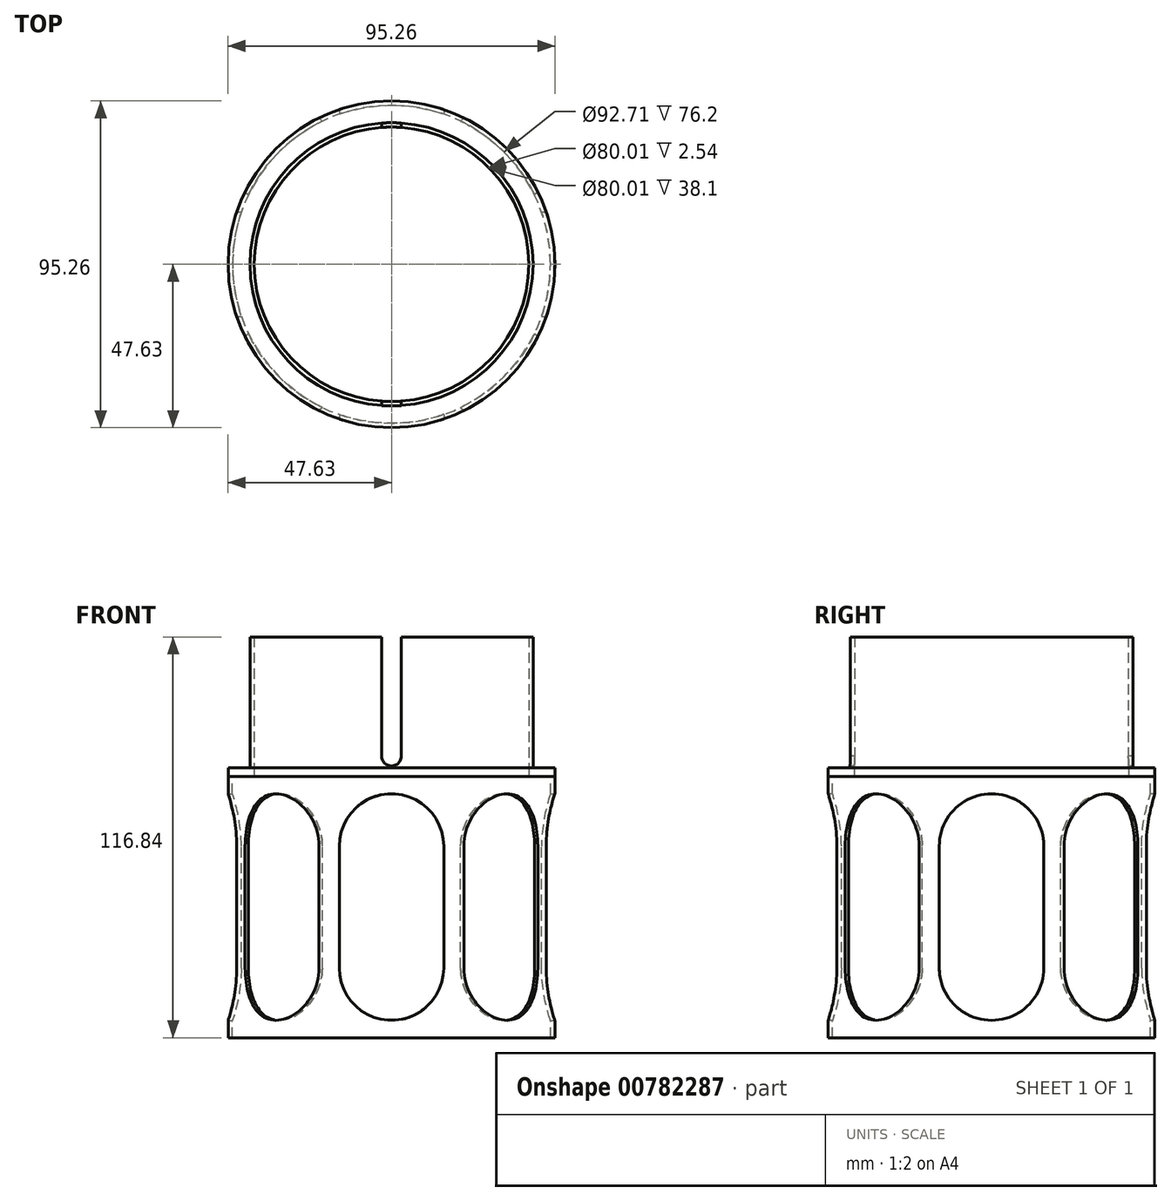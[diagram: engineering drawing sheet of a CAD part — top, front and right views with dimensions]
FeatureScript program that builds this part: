
annotation { "Feature Type Name" : "Feature", "Feature Type Description" : "" }
export const myFeature = defineFeature(function(context is Context, id is Id, definition is map)
    precondition{}
    {
        {
            var Q0;
            Q0=qCreatedBy(makeId("Top.planeOp"),FACE);
            var sketch = newSketch(context, id + "F0", { "sketchPlane" : qUnion([Q0])});
            skCircle(sketch, "E0", {"center": v(0, 0) * mm, "radius": 41.28 * mm});
            skCircle(sketch, "E1", {"center": v(0, 0) * mm, "radius": 40 * mm});
            skCircle(sketch, "E2", {"center": v(0, 0) * mm, "radius": 47.63 * mm});
            skCircle(sketch, "E3", {"center": v(0, 0) * mm, "radius": 46.35 * mm});
            skSolve(sketch);
        }
        {
            var Q0;
            Q0=makeQuery(id+"F0.imprint","IMPRINT",FACE,{"disambiguationData":[TD([[makeQuery(id+"F0.imprint","IMPRINT",EDGE,{"derivedFrom":sQuery(id+"F0.wireOp",EDGE,"E0")}),1.0]])]});
            extrude(context, id + "F1", {"entities" : qUnion([Q0]), "depth" : 40.64 * mm, "offsetDistance" : 25.4 * mm, "hasSecondDirection" : true, "secondDirectionOppositeDirection" : false, "secondDirectionDepth" : 2.54 * mm});
        }
        {
            var Q0;
            Q0=makeQuery(id+"F0.imprint","IMPRINT",FACE,{"disambiguationData":[TD([[makeQuery(id+"F0.imprint","IMPRINT",EDGE,{"derivedFrom":sQuery(id+"F0.wireOp",EDGE,"E2")}),1.0]])]});
            var Q1;
            Q1=sQuery(id+"F0.wireOp",EDGE,"E2");
            var Q2;
            Q2=sQuery(id+"F0.wireOp",EDGE,"E3");
            extrude(context, id + "F2", {"entities" : qUnion([Q0]), "surfaceEntities" : qUnion([Q1, Q2]), "oppositeDirection" : true, "depth" : 76.2 * mm, "offsetDistance" : 25.4 * mm});
        }
        {
            var Q0;
            Q0=makeQuery(id+"F0.imprint","IMPRINT",FACE,{"disambiguationData":[TD([[makeQuery(id+"F0.imprint","IMPRINT",EDGE,{"derivedFrom":sQuery(id+"F0.wireOp",EDGE,"E2")}),1.0]])]});
            var Q1;
            Q1=makeQuery(id+"F0.imprint","IMPRINT",FACE,{"disambiguationData":[TD([[makeQuery(id+"F0.imprint","IMPRINT",EDGE,{"derivedFrom":sQuery(id+"F0.wireOp",EDGE,"E0")}),-1.0]])]});
            var Q2;
            Q2=makeQuery(id+"F0.imprint","IMPRINT",FACE,{"disambiguationData":[TD([[makeQuery(id+"F0.imprint","IMPRINT",EDGE,{"derivedFrom":sQuery(id+"F0.wireOp",EDGE,"E0")}),1.0]])]});
            var Q3;
            Q3=sQuery(id+"F0.wireOp",EDGE,"E2");
            var Q4;
            Q4=sQuery(id+"F0.wireOp",EDGE,"E1");
            extrude(context, id + "F3", {"entities" : qUnion([Q0, Q1, Q2]), "surfaceEntities" : qUnion([Q3, Q4]), "depth" : 2.54 * mm, "offsetDistance" : 25.4 * mm});
        }
        {
            var Q0;
            Q0=qCreatedBy(makeId("Front.planeOp"),FACE);
            var sketch = newSketch(context, id + "F4", { "sketchPlane" : qUnion([Q0])});
            skCircle(sketch, "E4", {"center": v(0, -20.32) * mm, "radius": 15.24 * mm});
            skCircle(sketch, "E5", {"center": v(0, -55.89) * mm, "radius": 15.24 * mm});
            skLineSegment(sketch, "E6", {"start": v(-15.24, -55.89) * mm, "end": v(-15.24, -20.32) * mm});
            skLineSegment(sketch, "E7", {"start": v(15.24, -55.89) * mm, "end": v(15.24, -20.32) * mm});
            skCircle(sketch, "E8", {"center": v(0, 5.88) * mm, "radius": 2.84 * mm});
            skLineSegment(sketch, "E9", {"start": v(2.84, 5.88) * mm, "end": v(2.84, 40.64) * mm});
            skLineSegment(sketch, "E10", {"start": v(-2.84, 5.94) * mm, "end": v(-2.84, 40.64) * mm});
            skLineSegment(sketch, "E11", {"start": v(-2.84, 40.64) * mm, "end": v(2.84, 40.64) * mm});
            skSolve(sketch);
        }
        {
            var Q0;
            {var subQ0=sQuery(id+"F4.wireOp",EDGE,"E5");var subQ1=makeQuery(id+"F4.imprint","INTERSECT",VERTEX,{"derivedFrom":[subQ0,sQuery(id+"F4.wireOp",EDGE,"E6")]});Q0=makeQuery(id+"F4.imprint","IMPRINT",FACE,{"disambiguationData":[TD([[makeQuery(id+"F4.imprint","IMPRINT",EDGE,{"disambiguationData":[TD([[subQ1,1.0]])],"derivedFrom":subQ0}),1.0]])]});}
            var Q1;
            {var subQ0=sQuery(id+"F4.wireOp",EDGE,"E6");Q1=makeQuery(id+"F4.imprint","IMPRINT",FACE,{"disambiguationData":[TD([[makeQuery(id+"F4.imprint","IMPRINT",EDGE,{"derivedFrom":subQ0}),-1.0]])]});}
            var Q2;
            {var subQ0=sQuery(id+"F4.wireOp",EDGE,"E4");var subQ1=makeQuery(id+"F4.imprint","INTERSECT",VERTEX,{"derivedFrom":[subQ0,sQuery(id+"F4.wireOp",EDGE,"E6")]});Q2=makeQuery(id+"F4.imprint","IMPRINT",FACE,{"disambiguationData":[TD([[makeQuery(id+"F4.imprint","IMPRINT",EDGE,{"disambiguationData":[TD([[subQ1,1.0]])],"derivedFrom":subQ0}),1.0]])]});}
            var Q3;
            {var subQ0=sQuery(id+"F4.wireOp",EDGE,"E8");var subQ1=makeQuery(id+"F4.imprint","INTERSECT",VERTEX,{"derivedFrom":[subQ0,sQuery(id+"F4.wireOp",EDGE,"E9")]});Q3=makeQuery(id+"F4.imprint","IMPRINT",FACE,{"disambiguationData":[TD([[makeQuery(id+"F4.imprint","IMPRINT",EDGE,{"disambiguationData":[TD([[subQ1,-1.0]])],"derivedFrom":subQ0}),1.0]])]});}
            var Q4;
            {var subQ0=sQuery(id+"F4.wireOp",EDGE,"E9");Q4=makeQuery(id+"F4.imprint","IMPRINT",FACE,{"disambiguationData":[TD([[makeQuery(id+"F4.imprint","IMPRINT",EDGE,{"derivedFrom":subQ0}),1.0]])]});}
            extrude(context, id + "F5", {"entities" : qUnion([Q0, Q1, Q2, Q3, Q4]), "operationType" : NewBodyOperationType.REMOVE, "oppositeDirection" : true, "depth" : 76.2 * mm, "offsetDistance" : 25.4 * mm, "hasSecondDirection" : true, "secondDirectionOppositeDirection" : false, "secondDirectionDepth" : 76.2 * mm});
        }
        {
            var Q0;
            Q0=qCreatedBy(makeId("Right.planeOp"),FACE);
            var sketch = newSketch(context, id + "F6", { "sketchPlane" : qUnion([Q0])});
            skCircle(sketch, "E12", {"center": v(0, -20.32) * mm, "radius": 15.24 * mm});
            skCircle(sketch, "E13", {"center": v(0, -55.88) * mm, "radius": 15.24 * mm});
            skLineSegment(sketch, "E14", {"start": v(-15.24, -55.88) * mm, "end": v(-15.24, -20.32) * mm});
            skLineSegment(sketch, "E15", {"start": v(15.24, -55.88) * mm, "end": v(15.24, -20.32) * mm});
            skSolve(sketch);
        }
        {
            var Q0;
            Q0=qCreatedBy(makeId("Front.planeOp"),FACE);
            var Q1;
            Q1=qCreatedBy(makeId("Right.planeOp"),FACE);
            cPlane(context, id + "F7", {"entities" : qUnion([Q0, Q1]), "cplaneType" : CPlaneType.MID_PLANE, "offset" : 25.4 * mm, "width" : 152.4 * mm, "height" : 152.4 * mm});
        }
        {
            var Q0;
            Q0=qCreatedBy(id+"F7.planeOp",FACE);
            var sketch = newSketch(context, id + "F8", { "sketchPlane" : qUnion([Q0])});
            skCircle(sketch, "E16", {"center": v(0, -20.32) * mm, "radius": 15.24 * mm});
            skCircle(sketch, "E17", {"center": v(0, -55.88) * mm, "radius": 15.24 * mm});
            skLineSegment(sketch, "E18", {"start": v(-15.24, -55.88) * mm, "end": v(-15.24, -20.32) * mm});
            skLineSegment(sketch, "E19", {"start": v(15.24, -55.88) * mm, "end": v(15.24, -20.32) * mm});
            skSolve(sketch);
        }
        {
            var Q0;
            {var subQ0=sQuery(id+"F8.wireOp",EDGE,"E17");var subQ1=makeQuery(id+"F8.imprint","INTERSECT",VERTEX,{"derivedFrom":[subQ0,sQuery(id+"F8.wireOp",EDGE,"E18")]});Q0=makeQuery(id+"F8.imprint","IMPRINT",FACE,{"disambiguationData":[TD([[makeQuery(id+"F8.imprint","IMPRINT",EDGE,{"disambiguationData":[TD([[subQ1,1.0]])],"derivedFrom":subQ0}),1.0]])]});}
            var Q1;
            {var subQ0=sQuery(id+"F8.wireOp",EDGE,"E18");Q1=makeQuery(id+"F8.imprint","IMPRINT",FACE,{"disambiguationData":[TD([[makeQuery(id+"F8.imprint","IMPRINT",EDGE,{"derivedFrom":subQ0}),-1.0]])]});}
            var Q2;
            {var subQ0=sQuery(id+"F8.wireOp",EDGE,"E16");var subQ1=makeQuery(id+"F8.imprint","INTERSECT",VERTEX,{"derivedFrom":[subQ0,sQuery(id+"F8.wireOp",EDGE,"E18")]});Q2=makeQuery(id+"F8.imprint","IMPRINT",FACE,{"disambiguationData":[TD([[makeQuery(id+"F8.imprint","IMPRINT",EDGE,{"disambiguationData":[TD([[subQ1,1.0]])],"derivedFrom":subQ0}),1.0]])]});}
            var Q3;
            Q3=sQuery(id+"F8.wireOp",EDGE,"IbKOQnZK-ndt1-9ZTK-P8rp-GjTUkh9rXNRo");
            extrude(context, id + "F9", {"entities" : qUnion([Q0, Q1, Q2]), "operationType" : NewBodyOperationType.REMOVE, "surfaceEntities" : qUnion([Q3]), "oppositeDirection" : true, "depth" : 76.2 * mm, "offsetDistance" : 25.4 * mm, "hasSecondDirection" : true, "secondDirectionOppositeDirection" : false, "secondDirectionDepth" : 76.2 * mm});
        }
        {
            var Q0;
            Q0=qCreatedBy(makeId("Right.planeOp"),FACE);
            var Q1;
            Q1=qCreatedBy(makeId("Front.planeOp"),FACE);
            cPlane(context, id + "F10", {"entities" : qUnion([Q0, Q1]), "cplaneType" : CPlaneType.MID_PLANE, "offset" : 25.4 * mm, "flipAlignment" : true, "width" : 152.4 * mm, "height" : 152.4 * mm});
        }
        {
            var Q0;
            Q0=qCreatedBy(id+"F10.planeOp",FACE);
            var sketch = newSketch(context, id + "F11", { "sketchPlane" : qUnion([Q0])});
            skCircle(sketch, "E20", {"center": v(0, -20.32) * mm, "radius": 15.24 * mm});
            skCircle(sketch, "E21", {"center": v(0, -55.88) * mm, "radius": 15.24 * mm});
            skLineSegment(sketch, "E22", {"start": v(-15.24, -55.88) * mm, "end": v(-15.24, -20.32) * mm});
            skLineSegment(sketch, "E23", {"start": v(15.24, -55.88) * mm, "end": v(15.24, -20.32) * mm});
            skSolve(sketch);
        }
        {
            var Q0;
            {var subQ0=sQuery(id+"F11.wireOp",EDGE,"E21");var subQ1=makeQuery(id+"F11.imprint","INTERSECT",VERTEX,{"derivedFrom":[subQ0,sQuery(id+"F11.wireOp",EDGE,"E22")]});Q0=makeQuery(id+"F11.imprint","IMPRINT",FACE,{"disambiguationData":[TD([[makeQuery(id+"F11.imprint","IMPRINT",EDGE,{"disambiguationData":[TD([[subQ1,1.0]])],"derivedFrom":subQ0}),1.0]])]});}
            var Q1;
            {var subQ0=sQuery(id+"F11.wireOp",EDGE,"E22");Q1=makeQuery(id+"F11.imprint","IMPRINT",FACE,{"disambiguationData":[TD([[makeQuery(id+"F11.imprint","IMPRINT",EDGE,{"derivedFrom":subQ0}),-1.0]])]});}
            var Q2;
            {var subQ0=sQuery(id+"F11.wireOp",EDGE,"E20");var subQ1=makeQuery(id+"F11.imprint","INTERSECT",VERTEX,{"derivedFrom":[subQ0,sQuery(id+"F11.wireOp",EDGE,"E22")]});Q2=makeQuery(id+"F11.imprint","IMPRINT",FACE,{"disambiguationData":[TD([[makeQuery(id+"F11.imprint","IMPRINT",EDGE,{"disambiguationData":[TD([[subQ1,1.0]])],"derivedFrom":subQ0}),1.0]])]});}
            var Q3;
            Q3=sQuery(id+"F11.wireOp",EDGE,"P5bQX13I-b14g-q5Ht-MTCa-6Y4vRfw4qNGV");
            extrude(context, id + "F12", {"entities" : qUnion([Q0, Q1, Q2]), "operationType" : NewBodyOperationType.REMOVE, "surfaceEntities" : qUnion([Q3]), "oppositeDirection" : true, "depth" : 76.2 * mm, "offsetDistance" : 25.4 * mm, "hasSecondDirection" : true, "secondDirectionOppositeDirection" : false, "secondDirectionDepth" : 76.2 * mm});
        }
        {
            var Q0;
            Q0 = qSketchRegion(id + "F6", true);
            extrude(context, id + "F13", {"entities" : qUnion([Q0]), "operationType" : NewBodyOperationType.REMOVE, "oppositeDirection" : true, "depth" : 76.2 * mm, "offsetDistance" : 25.4 * mm, "hasSecondDirection" : true, "secondDirectionOppositeDirection" : false, "secondDirectionDepth" : 76.2 * mm});
        }
    });
